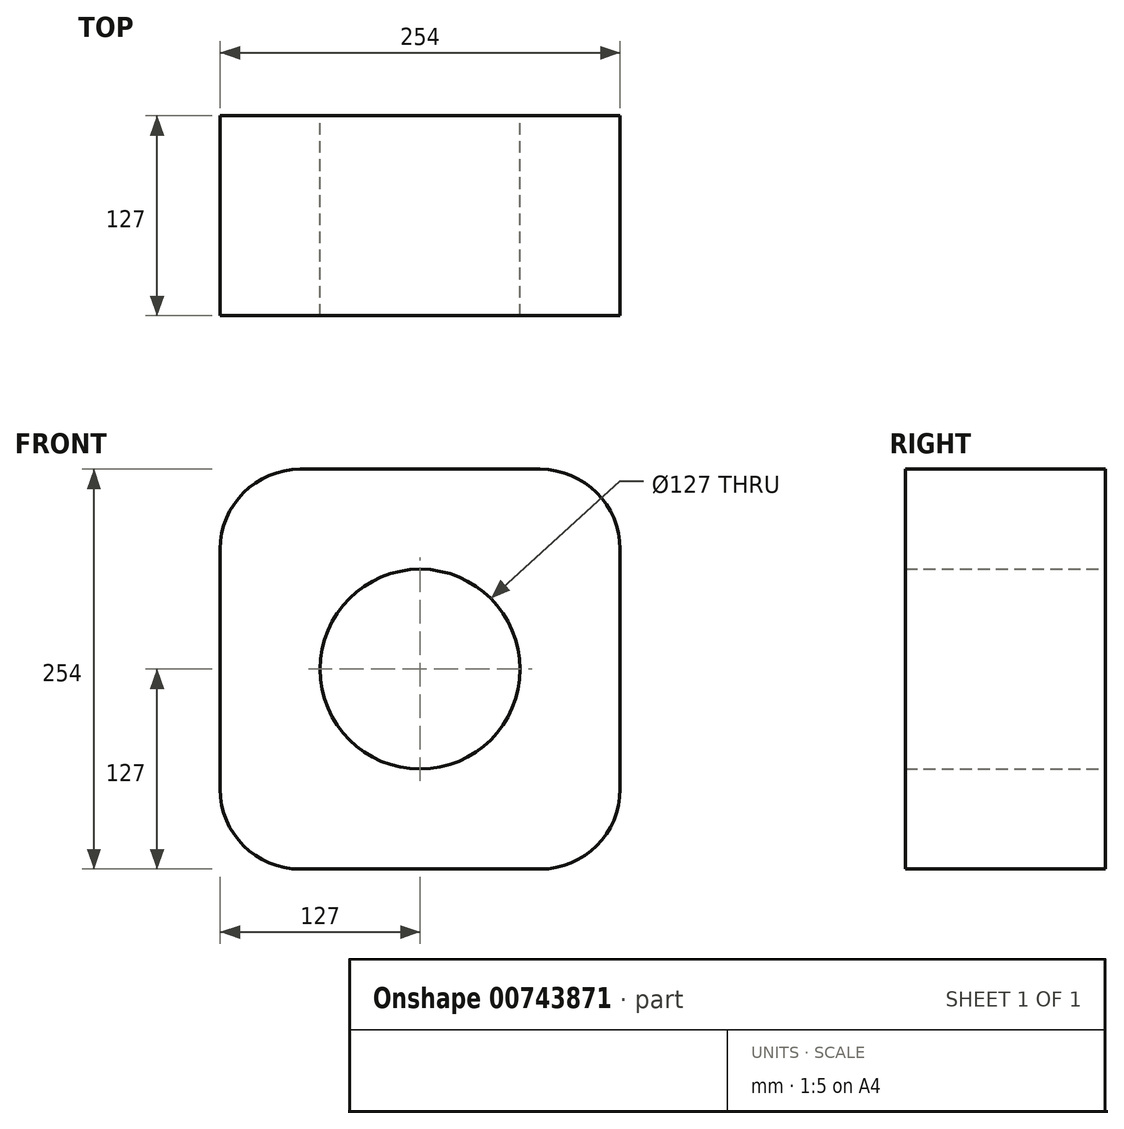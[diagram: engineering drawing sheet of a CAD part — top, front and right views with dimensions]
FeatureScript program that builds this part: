
annotation { "Feature Type Name" : "Feature", "Feature Type Description" : "" }
export const myFeature = defineFeature(function(context is Context, id is Id, definition is map)
    precondition{}
    {
        {
            var Q0;
            Q0=qCreatedBy(makeId("Front.planeOp"),FACE);
            var sketch = newSketch(context, id + "F0", { "sketchPlane" : qUnion([Q0])});
            skLineSegment(sketch, "E0", {"start": v(50.8, 0) * mm, "end": v(203.2, 0) * mm});
            skLineSegment(sketch, "E1", {"start": v(254, 50.8) * mm, "end": v(254, 203.2) * mm});
            skLineSegment(sketch, "E2", {"start": v(203.2, 254) * mm, "end": v(50.8, 254) * mm});
            skLineSegment(sketch, "E3", {"start": v(0, 203.2) * mm, "end": v(0, 50.8) * mm});
            skCircle(sketch, "E4", {"center": v(127, 127) * mm, "radius": 63.5 * mm});
            skPoint(sketch, "E5.visualSharp", {"position": v(0, 254) * mm});
            skArc(sketch, "E5.filletArc", {"start": v(50.8, 254) * mm, "mid": v(14.88, 239.12) * mm, "end": v(0, 203.2) * mm});
            skPoint(sketch, "E6.visualSharp", {"position": v(254, 254) * mm});
            skArc(sketch, "E6.filletArc", {"start": v(254, 203.2) * mm, "mid": v(239.12, 239.12) * mm, "end": v(203.2, 254) * mm});
            skPoint(sketch, "E7.visualSharp", {"position": v(254, 0) * mm});
            skArc(sketch, "E7.filletArc", {"start": v(203.2, 0) * mm, "mid": v(239.12, 14.88) * mm, "end": v(254, 50.8) * mm});
            skPoint(sketch, "E8.visualSharp", {"position": v(0, 0) * mm});
            skArc(sketch, "E8.filletArc", {"start": v(0, 50.8) * mm, "mid": v(14.88, 14.88) * mm, "end": v(50.8, 0) * mm});
            skSolve(sketch);
        }
        {
            var Q0;
            Q0 = qSketchRegion(id + "F0", true);
            extrude(context, id + "F1", {"entities" : qUnion([Q0]), "depth" : 127 * mm, "offsetDistance" : 25.4 * mm});
        }
    });
